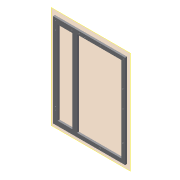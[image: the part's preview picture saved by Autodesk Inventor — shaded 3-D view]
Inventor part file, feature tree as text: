
AUTODESK INVENTOR PART (.ipt)
format: ipt  version: 2019.4 (Build 234330000, 330)  size: 121,856 bytes
history: native  units: mm
features: other x3, sketch x2, plane x1, extrude x1, hole x1
ambient origin geometry x8: Origin, YZ Plane, XZ Plane, XY Plane, X Axis, Y Axis, Z Axis, Center Point
bodies: Body1 (feature_tree)
feature tree (8):
  plane  "Work Plane3"
  extrude  "Extrusion3"  [1 undecoded]
  hole  "Hole2"  [1 undecoded]
  sketch  "Sketch6"  dims[d11=5.0mm d12=0.0mm]
  sketch  "Sketch7"  dims[d13=2.8mm d14=6.0mm d15=4.0mm d16=2.0mm d17=90.0deg d18=8.0mm d19=20.594885mm]
  other  "Assembly_Opentrons_Imagingunit_v3.iam"
  other  "Assembly_opentrons_microscope_slide_y_base:1"
  other  "02_Opentrons_Microscope_Base_v0:1"
note: 2 required parameter values undecoded (feature->parameter linkage not recoverable at this tier; creation-order binding heuristic only, values carry confidence <= 0.55)
